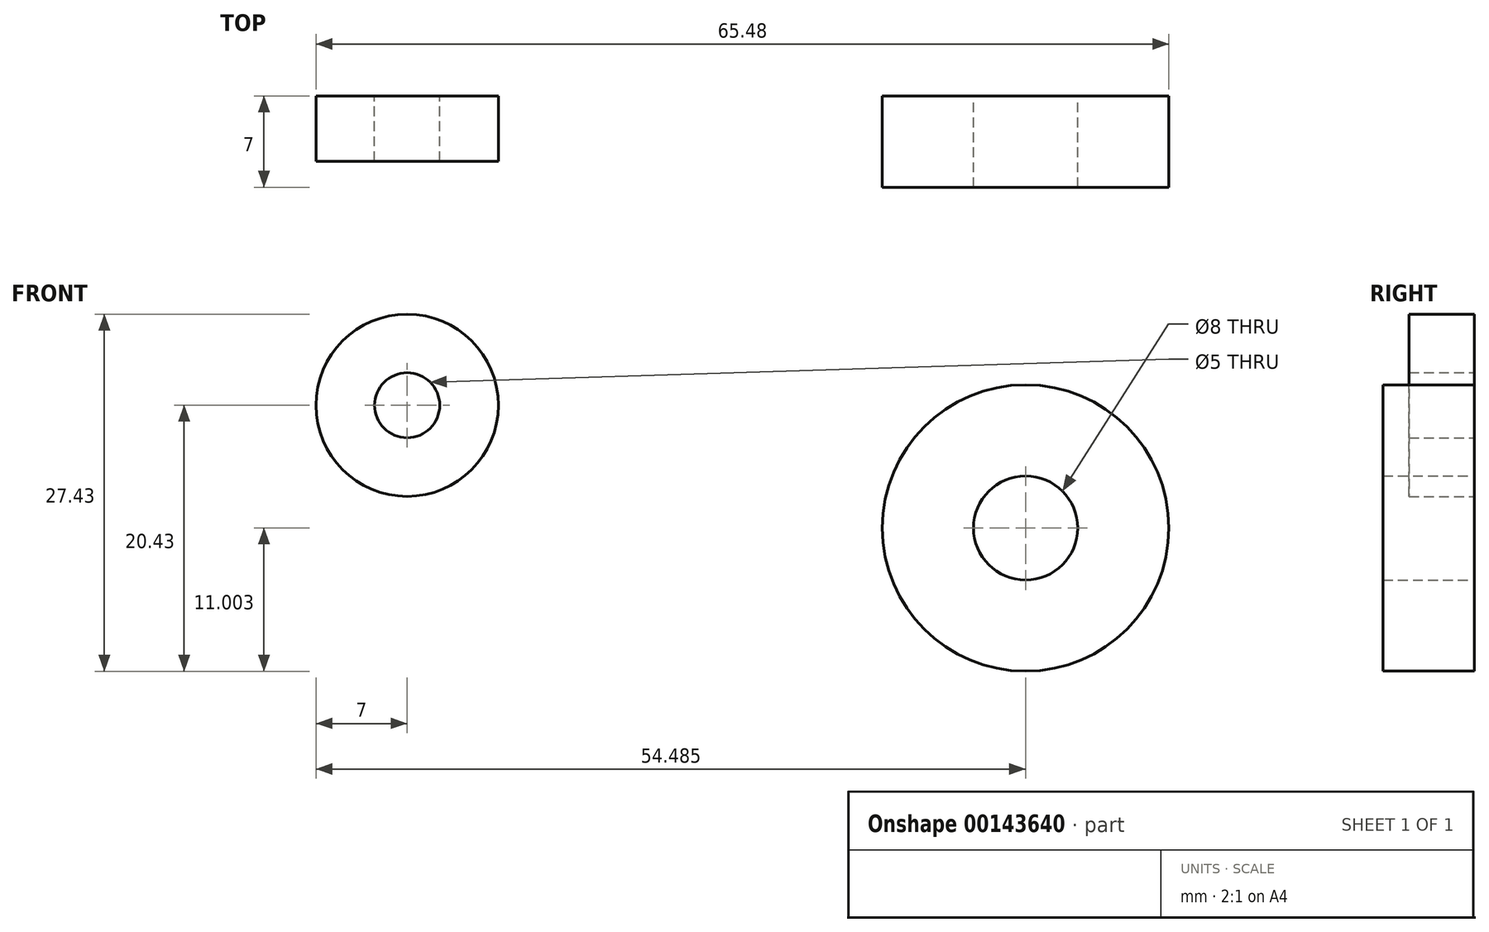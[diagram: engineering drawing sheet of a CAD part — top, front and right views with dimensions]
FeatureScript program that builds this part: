
annotation { "Feature Type Name" : "Feature", "Feature Type Description" : "" }
export const myFeature = defineFeature(function(context is Context, id is Id, definition is map)
    precondition{}
    {
        {
            var Q0;
            Q0=qCreatedBy(makeId("Front.planeOp"),FACE);
            var sketch = newSketch(context, id + "F0", { "sketchPlane" : qUnion([Q0])});
            skCircle(sketch, "E0", {"center": v(0, 0) * mm, "radius": 7 * mm});
            skCircle(sketch, "E1", {"center": v(0, 0) * mm, "radius": 2.5 * mm});
            skCircle(sketch, "E2", {"center": v(47.48, -9.43) * mm, "radius": 11 * mm});
            skCircle(sketch, "E3", {"center": v(47.48, -9.43) * mm, "radius": 4 * mm});
            skSolve(sketch);
        }
        {
            var Q0;
            Q0=makeQuery(id+"F0.imprint","IMPRINT",FACE,{"disambiguationData":[TD([[makeQuery(id+"F0.imprint","IMPRINT",EDGE,{"derivedFrom":sQuery(id+"F0.wireOp",EDGE,"E0")}),1.0]])]});
            extrude(context, id + "F1", {"entities" : qUnion([Q0]), "depth" : 5 * mm});
        }
        {
            var Q0;
            Q0=makeQuery(id+"F0.imprint","IMPRINT",FACE,{"disambiguationData":[TD([[makeQuery(id+"F0.imprint","IMPRINT",EDGE,{"derivedFrom":sQuery(id+"F0.wireOp",EDGE,"E2")}),1.0]])]});
            extrude(context, id + "F2", {"entities" : qUnion([Q0]), "depth" : 7 * mm});
        }
    });
